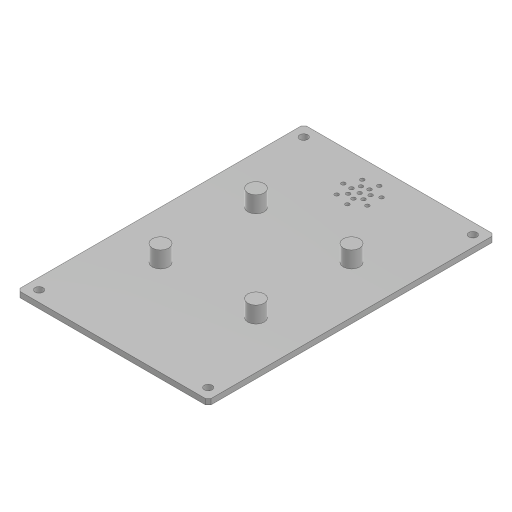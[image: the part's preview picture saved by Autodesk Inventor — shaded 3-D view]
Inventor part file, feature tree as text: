
AUTODESK INVENTOR PART (.ipt)
format: ipt  version: 2023.1 (Build 271208000, 208)  size: 204,800 bytes
history: native  units: mm
features: sketch x5, extrude x3, hole x3, projected_geometry x2, other x1, chamfer x1, pattern_circular x1
ambient origin geometry x8: Origin, YZ Plane, XZ Plane, XY Plane, X Axis, Y Axis, Z Axis, Center Point
bodies: Volumenkörper1 (feature_tree)
feature tree (16):
  other  "Case_bottom"
  extrude  "Extrusion1"  Depth=105.0mm
  hole  "Bohrung1"  [1 undecoded]
  extrude  "Extrusion5"  Depth=70.0mm
  extrude  "Extrusion6"  Depth=2.0mm
  hole  "Bohrung2"  [1 undecoded]
  chamfer  "Fase1"  Distance=20.0mm
  hole  "Bohrung3"  [1 undecoded]
  pattern_circular  "Runde Anordnung1"  [2 undecoded]
  sketch  "Skizze1"  dims[d0=70.0mm d1=105.0mm]
  sketch  "Skizze3"  dims[d2=2.0mm d3=0.0mm d27=105.0mm]
  projected_geometry  "Projizierte Kontur2"
  projected_geometry  "Projizierte Kontur4"
  sketch  "Skizze6"  dims[d28=70.0mm d29=62.0mm]
  sketch  "Skizze7"  dims[d30=97.0mm]
  sketch  "Skizze10"  dims[d31=3.0mm d32=6.0mm d33=4.0mm d34=2.0mm d35=90.0deg d36=8.0mm d37=20.594885mm d45=2.0mm d46=42.0mm d48=20.0mm d49=7.0mm d51=0.0mm d52=15.0mm d53=0.0mm d56=10.0mm d57=3.0mm d58=20.0mm d59=0.0mm d60=35.0mm d61=6.0mm d62=6.0mm d63=6.0mm d64=6.0mm d65=6.0mm d66=0.0mm d67=2.5mm d68=6.0mm d69=4.0mm d70=2.0mm d71=90.0deg d72=5.0mm d73=20.594885mm d95=1.0mm d96=2.0mm d97=45.0deg d98=1.5mm d99=6.0mm d100=4.0mm d101=2.0mm d102=90.0deg d103=5.0mm d104=20.594885mm d105=41.0mm d106=3.0mm d107=3.0mm d108=3.0mm d109=70.0mm d110=360.0deg]
note: 5 required parameter values undecoded (feature->parameter linkage not recoverable at this tier; creation-order binding heuristic only, values carry confidence <= 0.55)
